# Revit family: Specialty_Equipment-Fiberstone_Planter-Planters_Unlimited-Aurelius-Round
name_source: partatom
category: Specialty Equipment
units: mm (PartAtom-declared; Revit-internal decimal feet)

## family parameters
Always vertical = Yes
Cut with Voids When Loaded = No
Enable Cutting in Views = No
Maintain Annotation Orientation = No
OmniClass Number = 23.40.05.21.17
OmniClass Title = Planters
Part Type = Normal
Room Calculation Point = No
Round Connector Dimension = Use Diameter
Shared = No
Work Plane-Based = No

## types (3) — shared parameters
Assembly Code = G2050600
CD_Finish = Plastic-Fiberstone-Carlsbad-Chenza
CD_Microsite = https://www.caddetails.com
CD_Pad Size = 3.0"
CD_Product Page URL = https://www.plantersunlimited.com
CD_Specification = https://www.plantersunlimited.com
Default Elevation = 0.0"
Description = Aurelius Round Planters
Manufacturer = Planters Unlimited
Model = Aurelius Round Planter
Type Comments = Round Planter
URL = https://www.plantersunlimited.com

## per-type parameters (varying)
| type | CD_Diameter | CD_Diameter Baseplate | CD_Diameter Lip | CD_Height |
| 26"Dia x 28"H | 26.0" | 13.0" | 22.0" | 28.0" |
| 36"Dia x 38"H | 36.0" | 18.0" | 32.0" | 38.0" |
| 48"Dia x 52"H | 48.0" | 24.0" | 44.0" | 52.0" |

## geometry (parser evidence)
native form markers: Sweep x3
no freeform markers — native parametric forms only
